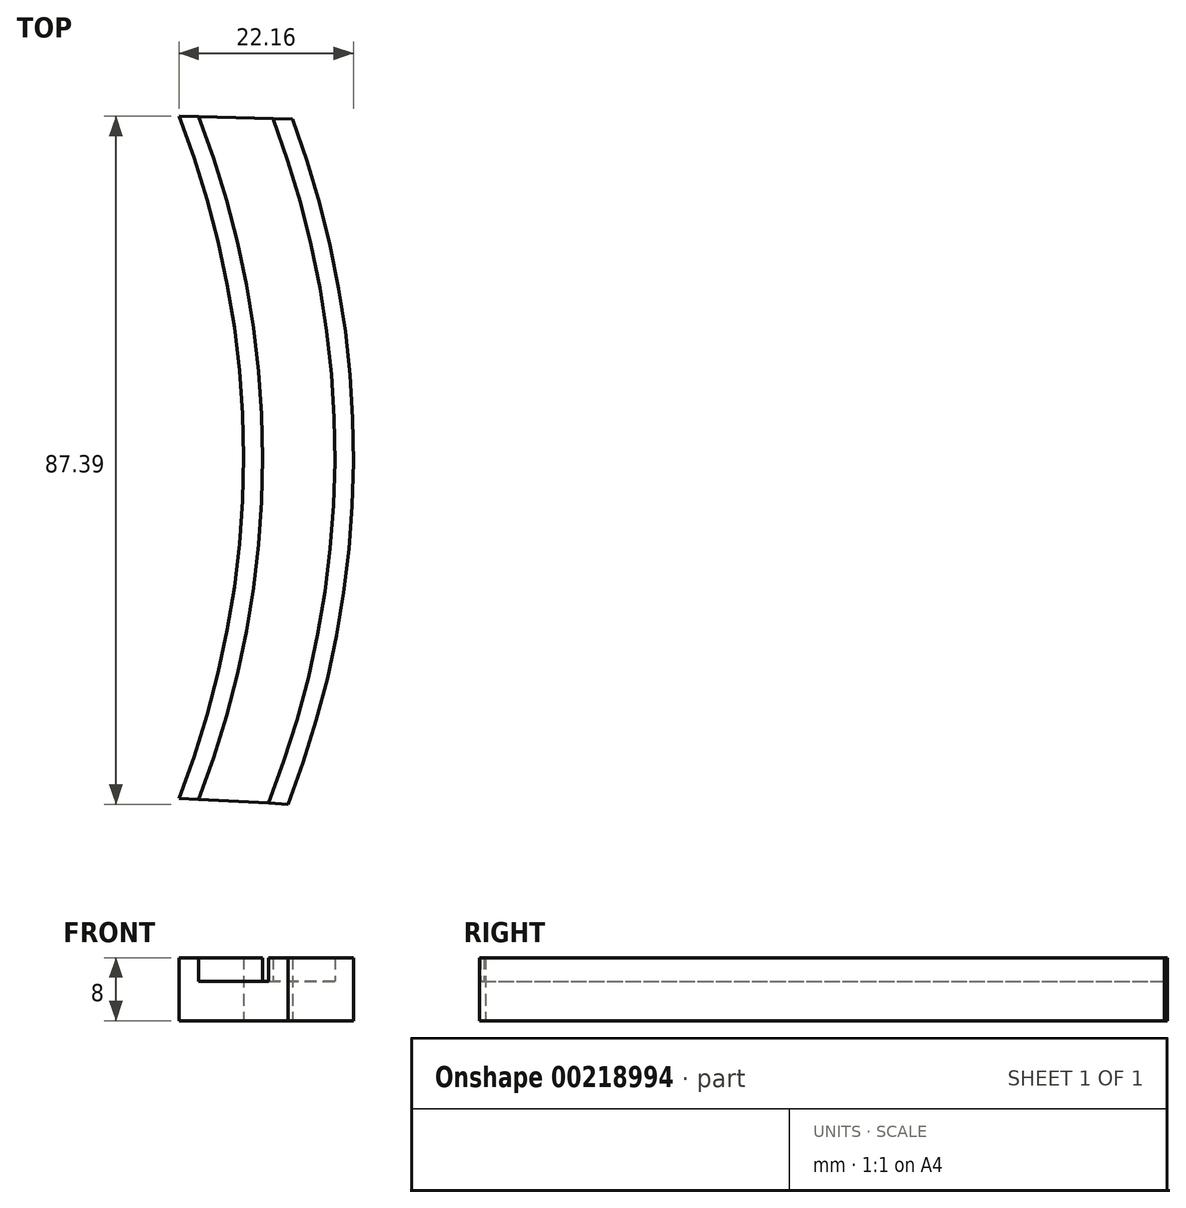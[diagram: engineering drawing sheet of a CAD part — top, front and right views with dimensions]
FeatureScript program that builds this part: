
annotation { "Feature Type Name" : "Feature", "Feature Type Description" : "" }
export const myFeature = defineFeature(function(context is Context, id is Id, definition is map)
    precondition{}
    {
        {
            var Q0;
            Q0=qCreatedBy(makeId("Top.planeOp"),FACE);
            var sketch = newSketch(context, id + "F0", { "sketchPlane" : qUnion([Q0])});
            skArc(sketch, "E0", {"start": v(4.75, -41.32) * mm, "mid": v(12.94, 2) * mm, "end": v(4.75, 45.31) * mm});
            skArc(sketch, "E1", {"start": v(18.62, -42.08) * mm, "mid": v(26.9, 1.37) * mm, "end": v(19.19, 44.93) * mm});
            skLineSegment(sketch, "E2", {"start": v(4.75, 45.31) * mm, "end": v(19.19, 44.93) * mm});
            skLineSegment(sketch, "E3", {"start": v(4.75, -41.32) * mm, "end": v(18.62, -42.08) * mm});
            skSolve(sketch);
        }
        {
            var Q0;
            Q0 = qSketchRegion(id + "F0", true);
            extrude(context, id + "F1", {"entities" : qUnion([Q0]), "depth" : 5 * mm});
        }
        {
            var Q0;
            Q0=makeQuery(id+"F1.opExtrude","CAP_FACE",FACE,{"disambiguationData":[OSD([sQuery(id+"F0.wireOp",EDGE,"E0"),sQuery(id+"F0.wireOp",EDGE,"E1"),sQuery(id+"F0.wireOp",EDGE,"E2"),sQuery(id+"F0.wireOp",EDGE,"E3")])],"isStart":false});
            var sketch = newSketch(context, id + "F2", { "sketchPlane" : qUnion([Q0])});
            skArc(sketch, "E4", {"start": v(7.25, -41.46) * mm, "mid": v(15.35, 1.9) * mm, "end": v(7.25, 45.25) * mm});
            skArc(sketch, "E5", {"start": v(16.12, -41.95) * mm, "mid": v(24.56, 1.47) * mm, "end": v(16.69, 45) * mm});
            skSolve(sketch);
        }
        {
            var Q0;
            {var subQ0=sQuery(id+"F2.wireOp",EDGE,"E4");Q0=makeQuery(id+"F2.imprint","IMPRINT",FACE,{"disambiguationData":[TD([[makeQuery(id+"F2.imprint","IMPRINT",EDGE,{"derivedFrom":subQ0}),1.0]])]});}
            var Q1;
            {var subQ0=sQuery(id+"F2.wireOp",EDGE,"E5");Q1=makeQuery(id+"F2.imprint","IMPRINT",FACE,{"disambiguationData":[TD([[makeQuery(id+"F2.imprint","IMPRINT",EDGE,{"derivedFrom":subQ0}),-1.0]])]});}
            extrude(context, id + "F3", {"entities" : qUnion([Q0, Q1]), "operationType" : NewBodyOperationType.ADD, "depth" : 3 * mm});
        }
    });
